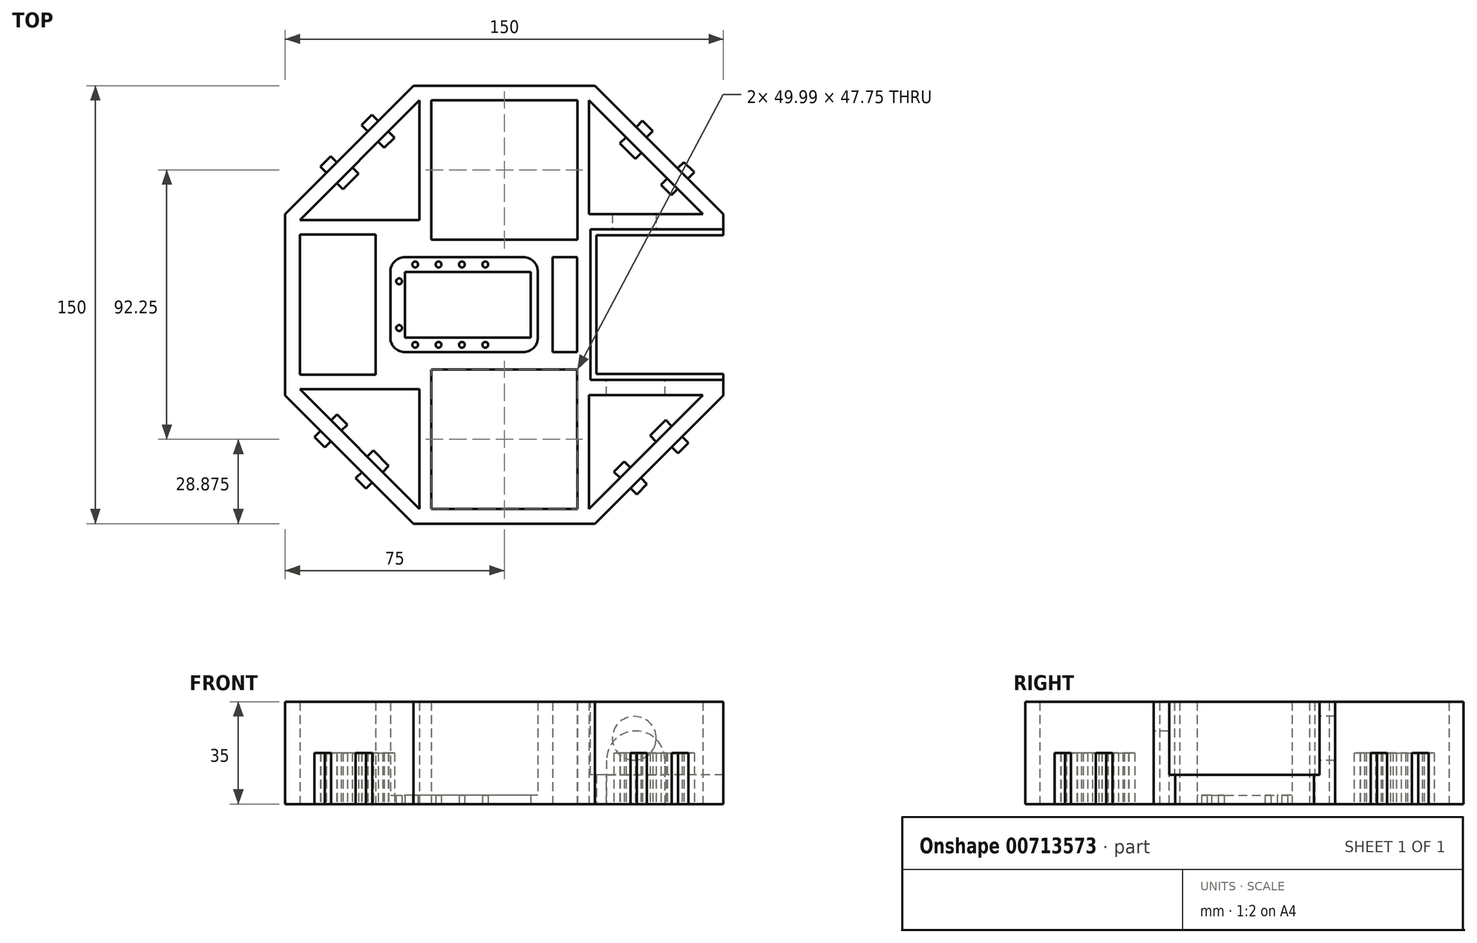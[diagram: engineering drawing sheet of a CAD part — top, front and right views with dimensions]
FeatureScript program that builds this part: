
annotation { "Feature Type Name" : "Feature", "Feature Type Description" : "" }
export const myFeature = defineFeature(function(context is Context, id is Id, definition is map)
    precondition{}
    {
        {
            var Q0;
            Q0=qCreatedBy(makeId("Top.planeOp"),FACE);
            var sketch = newSketch(context, id + "F0", { "sketchPlane" : qUnion([Q0])});
            skCircle(sketch, "E0.cCircle", {"center": v(0, 0) * mm, "radius": 75 * mm, "construction": true});
            skLineSegment(sketch, "E0.0", {"start": v(75, 31.07) * mm, "end": v(75, -31.07) * mm});
            skLineSegment(sketch, "E0.1", {"start": v(75, -31.07) * mm, "end": v(31.07, -75) * mm});
            skLineSegment(sketch, "E0.2", {"start": v(31.07, -75) * mm, "end": v(-31.07, -75) * mm});
            skLineSegment(sketch, "E0.3", {"start": v(-31.07, -75) * mm, "end": v(-75, -31.07) * mm});
            skLineSegment(sketch, "E0.4", {"start": v(-75, -31.07) * mm, "end": v(-75, 31.07) * mm});
            skLineSegment(sketch, "E0.5", {"start": v(-75, 31.07) * mm, "end": v(-31.07, 75) * mm});
            skLineSegment(sketch, "E0.6", {"start": v(-31.07, 75) * mm, "end": v(31.07, 75) * mm});
            skLineSegment(sketch, "E0.7", {"start": v(31.07, 75) * mm, "end": v(75, 31.07) * mm});
            skPoint(sketch, "E0.0.midPoint", {"position": v(75, 0) * mm});
            skLineSegment(sketch, "E1", {"start": v(0, 0) * mm, "end": v(11.5, 0) * mm, "construction": true});
            skLineSegment(sketch, "E2", {"start": v(11.5, 0) * mm, "end": v(11.5, -16.25) * mm});
            skLineSegment(sketch, "E3", {"start": v(11.5, 0) * mm, "end": v(11.5, 16.25) * mm});
            skLineSegment(sketch, "E4", {"start": v(11.5, 16.25) * mm, "end": v(-39, 16.25) * mm});
            skLineSegment(sketch, "E5", {"start": v(11.5, -16.25) * mm, "end": v(-39, -16.25) * mm});
            skLineSegment(sketch, "E6", {"start": v(-39, 16.25) * mm, "end": v(-39, -16.25) * mm});
            skSolve(sketch);
        }
        {
            var Q0;
            Q0=qSketchRegion(id+"F0",true);
            extrude(context, id + "F1", {"entities" : qUnion([Q0]), "depth" : 35 * mm});
        }
        {
            var Q0;
            Q0=makeQuery(id+"F1.opExtrude","CAP_FACE",FACE,{"disambiguationData":[OSD([sQuery(id+"F0.wireOp",EDGE,"E0.0"),sQuery(id+"F0.wireOp",EDGE,"E0.1"),sQuery(id+"F0.wireOp",EDGE,"E0.2"),sQuery(id+"F0.wireOp",EDGE,"E0.3"),sQuery(id+"F0.wireOp",EDGE,"E0.4"),sQuery(id+"F0.wireOp",EDGE,"E0.5"),sQuery(id+"F0.wireOp",EDGE,"E0.6"),sQuery(id+"F0.wireOp",EDGE,"E0.7"),sQuery(id+"F0.wireOp",EDGE,"E2"),sQuery(id+"F0.wireOp",EDGE,"E3"),sQuery(id+"F0.wireOp",EDGE,"E4"),sQuery(id+"F0.wireOp",EDGE,"E5"),sQuery(id+"F0.wireOp",EDGE,"E6")])],"isStart":true});
            var sketch = newSketch(context, id + "F2", { "sketchPlane" : qUnion([Q0])});
            skLineSegment(sketch, "E7.0", {"start": v(31.07, 75) * mm, "end": v(-31.07, 75) * mm});
            skLineSegment(sketch, "E7.1", {"start": v(-31.07, 75) * mm, "end": v(-75, 31.07) * mm});
            skLineSegment(sketch, "E7.2", {"start": v(-75, 31.07) * mm, "end": v(-75, -31.07) * mm});
            skLineSegment(sketch, "E7.3", {"start": v(-75, -31.07) * mm, "end": v(-31.07, -75) * mm});
            skLineSegment(sketch, "E7.4", {"start": v(-31.07, -75) * mm, "end": v(31.07, -75) * mm});
            skLineSegment(sketch, "E7.5", {"start": v(31.07, -75) * mm, "end": v(75, -31.07) * mm});
            skLineSegment(sketch, "E7.6", {"start": v(75, -31.07) * mm, "end": v(75, 31.07) * mm});
            skLineSegment(sketch, "E7.7", {"start": v(75, 31.07) * mm, "end": v(31.07, 75) * mm});
            skLineSegment(sketch, "E8.0", {"start": v(-29, 70) * mm, "end": v(-70, 29) * mm});
            skLineSegment(sketch, "E8.1", {"start": v(29, 70) * mm, "end": v(-29, 70) * mm, "construction": true});
            skLineSegment(sketch, "E8.2", {"start": v(-70, 29) * mm, "end": v(-70, -29) * mm, "construction": true});
            skLineSegment(sketch, "E8.3", {"start": v(70, 29) * mm, "end": v(68, 31) * mm, "construction": true});
            skLineSegment(sketch, "E8.4", {"start": v(-70, -29) * mm, "end": v(-29, -70) * mm});
            skLineSegment(sketch, "E8.5", {"start": v(-29, -70) * mm, "end": v(29, -70) * mm, "construction": true});
            skLineSegment(sketch, "E8.6", {"start": v(29, -70) * mm, "end": v(68, -31) * mm});
            skLineSegment(sketch, "E8.7", {"start": v(70, -29) * mm, "end": v(70, 29) * mm, "construction": true});
            skLineSegment(sketch, "E9.0", {"start": v(11.5, 16.25) * mm, "end": v(-39, 16.25) * mm, "construction": true});
            skLineSegment(sketch, "E9.1", {"start": v(-39, -16.25) * mm, "end": v(-39, 16.25) * mm, "construction": true});
            skLineSegment(sketch, "E9.2", {"start": v(11.5, -16.25) * mm, "end": v(-39, -16.25) * mm, "construction": true});
            skLineSegment(sketch, "E9.3", {"start": v(11.5, 16.25) * mm, "end": v(11.5, -16.25) * mm, "construction": true});
            skLineSegment(sketch, "E10", {"start": v(-70, 29) * mm, "end": v(-29, 29) * mm});
            skLineSegment(sketch, "E11", {"start": v(-29, 70) * mm, "end": v(-29, 29) * mm});
            skLineSegment(sketch, "E12", {"start": v(29, 70) * mm, "end": v(29, 31) * mm});
            skLineSegment(sketch, "E13", {"start": v(29, 29) * mm, "end": v(70, 29) * mm, "construction": true});
            skLineSegment(sketch, "E14", {"start": v(70, -29) * mm, "end": v(29, -29) * mm, "construction": true});
            skLineSegment(sketch, "E15", {"start": v(29, -29) * mm, "end": v(29, -31) * mm, "construction": true});
            skLineSegment(sketch, "E16", {"start": v(-29, -70) * mm, "end": v(-29, -29) * mm});
            skLineSegment(sketch, "E17", {"start": v(-29, -29) * mm, "end": v(-70, -29) * mm});
            skLineSegment(sketch, "E18", {"start": v(-25, 70) * mm, "end": v(25, 70) * mm});
            skLineSegment(sketch, "E19", {"start": v(0, 0) * mm, "end": v(27.89, 0) * mm, "construction": true});
            skPoint(sketch, "E19.endSnap0", {"position": v(11.5, 0) * mm});
            skLineSegment(sketch, "E20.MirrorCS", {"start": v(-25, -70) * mm, "end": v(25, -70) * mm});
            skLineSegment(sketch, "E21", {"start": v(-44, 24) * mm, "end": v(-44, -24) * mm});
            skLineSegment(sketch, "E22.0", {"start": v(68, -31) * mm, "end": v(29, -31) * mm});
            skLineSegment(sketch, "E23", {"start": v(29, -31) * mm, "end": v(29, -70) * mm});
            skLineSegment(sketch, "E24", {"start": v(68, -31) * mm, "end": v(70, -29) * mm, "construction": true});
            skLineSegment(sketch, "E25.0", {"start": v(29, 31) * mm, "end": v(68, 31) * mm});
            skLineSegment(sketch, "E26", {"start": v(29, 31) * mm, "end": v(29, 29) * mm, "construction": true});
            skLineSegment(sketch, "E27", {"start": v(68, 31) * mm, "end": v(29, 70) * mm});
            skLineSegment(sketch, "E28", {"start": v(-44, 24) * mm, "end": v(-70, 24) * mm});
            skLineSegment(sketch, "E29", {"start": v(-44, -24) * mm, "end": v(-70, -24) * mm});
            skLineSegment(sketch, "E30", {"start": v(-70, -24) * mm, "end": v(-70, 24) * mm});
            skLineSegment(sketch, "E31", {"start": v(-25, 22.25) * mm, "end": v(24.98, 22.25) * mm});
            skLineSegment(sketch, "E32", {"start": v(-25, -22.25) * mm, "end": v(25, -22.25) * mm});
            skLineSegment(sketch, "E33", {"start": v(-25, -22.25) * mm, "end": v(-25, -70) * mm});
            skLineSegment(sketch, "E34", {"start": v(25, -22.25) * mm, "end": v(25, -70) * mm});
            skLineSegment(sketch, "E35", {"start": v(24.98, 22.25) * mm, "end": v(25, 70) * mm});
            skLineSegment(sketch, "E36", {"start": v(-25, 22.25) * mm, "end": v(-25, 70) * mm});
            skLineSegment(sketch, "E37", {"start": v(16.5, 16.25) * mm, "end": v(16.5, -16.25) * mm});
            skLineSegment(sketch, "E38", {"start": v(16.5, 16.25) * mm, "end": v(24.98, 16.25) * mm});
            skLineSegment(sketch, "E39", {"start": v(24.98, 16.25) * mm, "end": v(24.98, -16.25) * mm});
            skLineSegment(sketch, "E40", {"start": v(24.98, -16.25) * mm, "end": v(16.5, -16.25) * mm});
            skSolve(sketch);
        }
        {
            var Q0;
            Q0=makeQuery(id+"F2.imprint","IMPRINT",FACE,{"disambiguationData":[TD([[makeQuery(id+"F2.imprint","IMPRINT",EDGE,{"derivedFrom":sQuery(id+"F2.wireOp",EDGE,"E8.0")}),1.0]])]});
            var Q1;
            Q1=makeQuery(id+"F2.imprint","IMPRINT",FACE,{"disambiguationData":[TD([[makeQuery(id+"F2.imprint","IMPRINT",EDGE,{"derivedFrom":sQuery(id+"F2.wireOp",EDGE,"E8.3")}),1.0]])]});
            var Q2;
            Q2=makeQuery(id+"F2.imprint","IMPRINT",FACE,{"disambiguationData":[TD([[makeQuery(id+"F2.imprint","IMPRINT",EDGE,{"derivedFrom":sQuery(id+"F2.wireOp",EDGE,"E8.4")}),1.0]])]});
            var Q3;
            Q3=makeQuery(id+"F2.imprint","IMPRINT",FACE,{"disambiguationData":[TD([[makeQuery(id+"F2.imprint","IMPRINT",EDGE,{"derivedFrom":sQuery(id+"F2.wireOp",EDGE,"8fvEKYef-Aid4-GxJZ-9eho-uKyJXPdf4iPF")}),1.0]])]});
            var Q4;
            Q4=makeQuery(id+"F2.imprint","IMPRINT",FACE,{"disambiguationData":[TD([[makeQuery(id+"F2.imprint","IMPRINT",EDGE,{"derivedFrom":sQuery(id+"F2.wireOp",EDGE,"9003354b-389c-4ee3-9b45-5ecd4443ff8f0.MirrorCS")}),-1.0]])]});
            var Q5;
            Q5=makeQuery(id+"F2.imprint","IMPRINT",FACE,{"disambiguationData":[TD([[makeQuery(id+"F2.imprint","IMPRINT",EDGE,{"derivedFrom":sQuery(id+"F2.wireOp",EDGE,"X22rCwxT-IPlS-Nedg-AixG-TADrHZbppUWM")}),-1.0]])]});
            var Q6;
            Q6=makeQuery(id+"F2.imprint","IMPRINT",FACE,{"disambiguationData":[TD([[makeQuery(id+"F2.imprint","IMPRINT",EDGE,{"derivedFrom":sQuery(id+"F2.wireOp",EDGE,"E12")}),1.0]])]});
            var Q7;
            Q7=makeQuery(id+"F2.imprint","IMPRINT",FACE,{"disambiguationData":[TD([[makeQuery(id+"F2.imprint","IMPRINT",EDGE,{"derivedFrom":sQuery(id+"F2.wireOp",EDGE,"E8.6")}),1.0]])]});
            var Q8;
            Q8=makeQuery(id+"F2.imprint","IMPRINT",FACE,{"disambiguationData":[TD([[makeQuery(id+"F2.imprint","IMPRINT",EDGE,{"derivedFrom":sQuery(id+"F2.wireOp",EDGE,"E21")}),-1.0]])]});
            var Q9;
            Q9=makeQuery(id+"F2.imprint","IMPRINT",FACE,{"disambiguationData":[TD([[makeQuery(id+"F2.imprint","IMPRINT",EDGE,{"derivedFrom":sQuery(id+"F2.wireOp",EDGE,"E18")}),-1.0]])]});
            var Q10;
            Q10=makeQuery(id+"F2.imprint","IMPRINT",FACE,{"disambiguationData":[TD([[makeQuery(id+"F2.imprint","IMPRINT",EDGE,{"derivedFrom":sQuery(id+"F2.wireOp",EDGE,"E20.MirrorCS")}),1.0]])]});
            var Q11;
            Q11=makeQuery(id+"F2.imprint","IMPRINT",FACE,{"disambiguationData":[TD([[makeQuery(id+"F2.imprint","IMPRINT",EDGE,{"derivedFrom":sQuery(id+"F2.wireOp",EDGE,"E37")}),1.0]])]});
            extrude(context, id + "F3", {"entities" : qUnion([Q0, Q1, Q2, Q3, Q4, Q5, Q6, Q7, Q8, Q9, Q10, Q11]), "operationType" : NewBodyOperationType.REMOVE, "oppositeDirection" : true, "depth" : 36.9 * mm});
        }
        {
            var Q0;
            Q0=makeQuery(id+"F1.opExtrude","CAP_FACE",FACE,{"disambiguationData":[OSD([sQuery(id+"F0.wireOp",EDGE,"E0.0"),sQuery(id+"F0.wireOp",EDGE,"E0.1"),sQuery(id+"F0.wireOp",EDGE,"E0.2"),sQuery(id+"F0.wireOp",EDGE,"E0.3"),sQuery(id+"F0.wireOp",EDGE,"E0.4"),sQuery(id+"F0.wireOp",EDGE,"E0.5"),sQuery(id+"F0.wireOp",EDGE,"E0.6"),sQuery(id+"F0.wireOp",EDGE,"E0.7"),sQuery(id+"F0.wireOp",EDGE,"E2"),sQuery(id+"F0.wireOp",EDGE,"E3"),sQuery(id+"F0.wireOp",EDGE,"E4"),sQuery(id+"F0.wireOp",EDGE,"E5"),sQuery(id+"F0.wireOp",EDGE,"E6")])],"isStart":true});
            var sketch = newSketch(context, id + "F4", { "sketchPlane" : qUnion([Q0])});
            skLineSegment(sketch, "E41.0", {"start": v(-39, -16.25) * mm, "end": v(-39, 16.25) * mm});
            skLineSegment(sketch, "E41.1", {"start": v(11.5, 16.25) * mm, "end": v(-39, 16.25) * mm});
            skLineSegment(sketch, "E41.2", {"start": v(11.5, -16.25) * mm, "end": v(-39, -16.25) * mm});
            skLineSegment(sketch, "E41.3", {"start": v(11.5, 16.25) * mm, "end": v(11.5, -16.25) * mm});
            skLineSegment(sketch, "E42.0", {"start": v(9, -11.25) * mm, "end": v(-34, -11.25) * mm});
            skLineSegment(sketch, "E42.1", {"start": v(-34, -11.25) * mm, "end": v(-34, 11.25) * mm});
            skLineSegment(sketch, "E42.2", {"start": v(9, 11.25) * mm, "end": v(-34, 11.25) * mm});
            skLineSegment(sketch, "E43", {"start": v(-39, 13.75) * mm, "end": v(-30.5, 13.75) * mm, "construction": true});
            skLineSegment(sketch, "E44", {"start": v(-30.5, 13.75) * mm, "end": v(-22.5, 13.75) * mm, "construction": true});
            skLineSegment(sketch, "E45", {"start": v(-22.5, 13.75) * mm, "end": v(-14.5, 13.75) * mm, "construction": true});
            skLineSegment(sketch, "E46", {"start": v(-14.5, 13.75) * mm, "end": v(-6.5, 13.75) * mm, "construction": true});
            skCircle(sketch, "E47", {"center": v(-30.5, 13.75) * mm, "radius": 1 * mm});
            skCircle(sketch, "E48", {"center": v(-22.5, 13.75) * mm, "radius": 1 * mm});
            skCircle(sketch, "E49", {"center": v(-14.5, 13.75) * mm, "radius": 1 * mm});
            skCircle(sketch, "E50", {"center": v(-6.5, 13.75) * mm, "radius": 1 * mm});
            skLineSegment(sketch, "E51", {"start": v(-39, 0) * mm, "end": v(-36, 0) * mm, "construction": true});
            skPoint(sketch, "E51.endSnap0", {"position": v(-39, 0) * mm});
            skLineSegment(sketch, "E52", {"start": v(-36, 0) * mm, "end": v(-36, 8) * mm, "construction": true});
            skLineSegment(sketch, "E53", {"start": v(-36, 0) * mm, "end": v(-36, -8) * mm, "construction": true});
            skLineSegment(sketch, "E54.MirrorCS", {"start": v(-39, -13.75) * mm, "end": v(-30.5, -13.75) * mm, "construction": true});
            skLineSegment(sketch, "E55.MirrorCS", {"start": v(-14.5, -13.75) * mm, "end": v(-6.5, -13.75) * mm, "construction": true});
            skCircle(sketch, "E56.MirrorC", {"center": v(-22.5, -13.75) * mm, "radius": 1 * mm});
            skCircle(sketch, "E57.MirrorC", {"center": v(-6.5, -13.75) * mm, "radius": 1 * mm});
            skCircle(sketch, "E58.MirrorC", {"center": v(-30.5, -13.75) * mm, "radius": 1 * mm});
            skLineSegment(sketch, "E59.MirrorCS", {"start": v(-30.5, -13.75) * mm, "end": v(-22.5, -13.75) * mm, "construction": true});
            skLineSegment(sketch, "E60.MirrorCS", {"start": v(-22.5, -13.75) * mm, "end": v(-14.5, -13.75) * mm, "construction": true});
            skCircle(sketch, "E61.MirrorC", {"center": v(-14.5, -13.75) * mm, "radius": 1 * mm});
            skCircle(sketch, "E62", {"center": v(-36, 8) * mm, "radius": 1 * mm});
            skCircle(sketch, "E63", {"center": v(-36, -8) * mm, "radius": 1 * mm});
            skLineSegment(sketch, "E64.0", {"start": v(9, 11.25) * mm, "end": v(9, -11.25) * mm});
            skSolve(sketch);
        }
        {
            var Q0;
            Q0=makeQuery(id+"F4.imprint","IMPRINT",FACE,{"disambiguationData":[TD([[makeQuery(id+"F4.imprint","IMPRINT",EDGE,{"derivedFrom":sQuery(id+"F4.wireOp",EDGE,"E41.0")}),-1.0]])]});
            extrude(context, id + "F5", {"entities" : qUnion([Q0]), "operationType" : NewBodyOperationType.ADD, "oppositeDirection" : true, "depth" : 3 * mm});
        }
        {
            var Q0;
            Q0=makeQuery(id+"F1.opExtrude","SWEPT_EDGE",EDGE,{"disambiguationData":[OSD([sQuery(id+"F0.wireOp",EDGE,"E5"),sQuery(id+"F0.wireOp",EDGE,"E6")])]});
            var Q1;
            Q1=makeQuery(id+"F1.opExtrude","SWEPT_EDGE",EDGE,{"disambiguationData":[OSD([sQuery(id+"F0.wireOp",EDGE,"E4"),sQuery(id+"F0.wireOp",EDGE,"E6")])]});
            var Q2;
            Q2=makeQuery(id+"F1.opExtrude","SWEPT_EDGE",EDGE,{"disambiguationData":[OSD([sQuery(id+"F0.wireOp",EDGE,"E3"),sQuery(id+"F0.wireOp",EDGE,"E4")])]});
            var Q3;
            Q3=makeQuery(id+"F1.opExtrude","SWEPT_EDGE",EDGE,{"disambiguationData":[OSD([sQuery(id+"F0.wireOp",EDGE,"E2"),sQuery(id+"F0.wireOp",EDGE,"E5")])]});
            fillet(context, id + "F6", {"entities" : qUnion([Q0, Q1, Q2, Q3]), "radius" : 5 * mm, "tangentPropagation" : true, "allowEdgeOverflow" : false});
        }
        {
            var Q0;
            Q0=makeQuery(id+"F1.opExtrude","CAP_FACE",FACE,{"disambiguationData":[OSD([sQuery(id+"F0.wireOp",EDGE,"E0.0"),sQuery(id+"F0.wireOp",EDGE,"E0.1"),sQuery(id+"F0.wireOp",EDGE,"E0.2"),sQuery(id+"F0.wireOp",EDGE,"E0.3"),sQuery(id+"F0.wireOp",EDGE,"E0.4"),sQuery(id+"F0.wireOp",EDGE,"E0.5"),sQuery(id+"F0.wireOp",EDGE,"E0.6"),sQuery(id+"F0.wireOp",EDGE,"E0.7"),sQuery(id+"F0.wireOp",EDGE,"E2"),sQuery(id+"F0.wireOp",EDGE,"E3"),sQuery(id+"F0.wireOp",EDGE,"E4"),sQuery(id+"F0.wireOp",EDGE,"E5"),sQuery(id+"F0.wireOp",EDGE,"E6")])],"isStart":false});
            var sketch = newSketch(context, id + "F7", { "sketchPlane" : qUnion([Q0])});
            skLineSegment(sketch, "E65.bottom", {"start": v(75, -25.75) * mm, "end": v(29.5, -25.75) * mm});
            skLineSegment(sketch, "E65.top", {"start": v(75, 25.75) * mm, "end": v(29.5, 25.75) * mm});
            skLineSegment(sketch, "E65.right", {"start": v(29.5, -25.75) * mm, "end": v(29.5, 25.75) * mm});
            skPoint(sketch, "E65.middle", {"position": v(52.25, 0) * mm});
            skPoint(sketch, "E66", {"position": v(75, 0) * mm});
            skLineSegment(sketch, "E67", {"start": v(75, 0) * mm, "end": v(52.25, 0) * mm, "construction": true});
            skSolve(sketch);
        }
        {
            var Q0;
            {var subQ0=sQuery(id+"F7.wireOp",EDGE,"E65.bottom");Q0=makeQuery(id+"F7.imprint","IMPRINT",FACE,{"disambiguationData":[TD([[makeQuery(id+"F7.imprint","IMPRINT",EDGE,{"derivedFrom":subQ0}),-1.0]])]});}
            extrude(context, id + "F8", {"entities" : qUnion([Q0]), "operationType" : NewBodyOperationType.REMOVE, "oppositeDirection" : true, "depth" : 30 * mm});
        }
        {
            var Q0;
            Q0=makeQuery(id+"F8.boolean.opBoolean","COPY",FACE,{"derivedFrom":makeQuery(id+"F8.opExtrude","CAP_FACE",FACE,{"disambiguationData":[OSD([sQuery(id+"F0.wireOp",EDGE,"E0.0"),sQuery(id+"F7.wireOp",EDGE,"E65.bottom"),sQuery(id+"F7.wireOp",EDGE,"E65.top"),sQuery(id+"F7.wireOp",EDGE,"E65.right")])],"isStart":false})});
            var sketch = newSketch(context, id + "F9", { "sketchPlane" : qUnion([Q0])});
            skLineSegment(sketch, "E68.0", {"start": v(75, 25.75) * mm, "end": v(29.5, 25.75) * mm});
            skLineSegment(sketch, "E68.1", {"start": v(29.5, -25.75) * mm, "end": v(29.5, 25.75) * mm});
            skLineSegment(sketch, "E68.2", {"start": v(75, -25.75) * mm, "end": v(29.5, -25.75) * mm});
            skLineSegment(sketch, "E69.0", {"start": v(75, -23.75) * mm, "end": v(31.5, -23.75) * mm});
            skLineSegment(sketch, "E69.1", {"start": v(31.5, -23.75) * mm, "end": v(31.5, 23.75) * mm});
            skLineSegment(sketch, "E69.2", {"start": v(75, 23.75) * mm, "end": v(31.5, 23.75) * mm});
            skLineSegment(sketch, "E70", {"start": v(75, 23.75) * mm, "end": v(75, 25.75) * mm});
            skLineSegment(sketch, "E71", {"start": v(75, -23.75) * mm, "end": v(75, -25.75) * mm});
            skSolve(sketch);
        }
        {
            var Q0;
            Q0=makeQuery(id+"F9.imprint","IMPRINT",FACE,{"disambiguationData":[TD([[makeQuery(id+"F9.imprint","IMPRINT",EDGE,{"derivedFrom":sQuery(id+"F9.wireOp",EDGE,"E68.0")}),1.0]])]});
            extrude(context, id + "F10", {"entities" : qUnion([Q0]), "operationType" : NewBodyOperationType.ADD, "depth" : 5 * mm});
        }
        {
            var Q0;
            Q0=makeQuery(id+"F8.boolean.opBoolean","COPY",FACE,{"derivedFrom":makeQuery(id+"F8.opExtrude","SWEPT_FACE",FACE,{"disambiguationData":[OSD([sQuery(id+"F7.wireOp",EDGE,"E65.bottom")])]})});
            var sketch = newSketch(context, id + "F11", { "sketchPlane" : qUnion([Q0])});
            skLineSegment(sketch, "E72.0", {"start": v(-68, 35) * mm, "end": v(-68, 0) * mm, "construction": true});
            skLineSegment(sketch, "E73", {"start": v(-55, 10) * mm, "end": v(-55, 25) * mm});
            skLineSegment(sketch, "E74", {"start": v(-55, 25) * mm, "end": v(-35, 25) * mm});
            skLineSegment(sketch, "E75", {"start": v(-35, 25) * mm, "end": v(-35, 10) * mm});
            skLineSegment(sketch, "E76", {"start": v(-35, 10) * mm, "end": v(-55, 10) * mm});
            skSolve(sketch);
        }
        {
            var Q0;
            Q0=makeQuery(id+"F11.imprint","IMPRINT",FACE,{"disambiguationData":[TD([[makeQuery(id+"F11.imprint","IMPRINT",EDGE,{"derivedFrom":sQuery(id+"F11.wireOp",EDGE,"E73")}),-1.0]])]});
            extrude(context, id + "F12", {"entities" : qUnion([Q0]), "operationType" : NewBodyOperationType.REMOVE, "oppositeDirection" : true, "depth" : 11.4 * mm});
        }
        {
            var Q0;
            Q0=makeQuery(id+"F12.boolean.opBoolean","COPY",EDGE,{"derivedFrom":makeQuery(id+"F12.opExtrude","SWEPT_EDGE",EDGE,{"disambiguationData":[OSD([sQuery(id+"F11.wireOp",EDGE,"E73"),sQuery(id+"F11.wireOp",EDGE,"E74")])]})});
            var Q1;
            Q1=makeQuery(id+"F12.boolean.opBoolean","COPY",EDGE,{"derivedFrom":makeQuery(id+"F12.opExtrude","SWEPT_EDGE",EDGE,{"disambiguationData":[OSD([sQuery(id+"F11.wireOp",EDGE,"E74"),sQuery(id+"F11.wireOp",EDGE,"E75")])]})});
            fillet(context, id + "F13", {"entities" : qUnion([Q0, Q1]), "radius" : 10 * mm, "tangentPropagation" : true, "allowEdgeOverflow" : false});
        }
        {
            var Q0;
            Q0=makeQuery(id+"F12.boolean.opBoolean","MERGE",FACE,{"derivedFrom":[makeQuery(id+"F10.opExtrude","CAP_FACE",FACE,{"disambiguationData":[OSD([sQuery(id+"F9.wireOp",EDGE,"E68.0"),sQuery(id+"F9.wireOp",EDGE,"E68.1"),sQuery(id+"F9.wireOp",EDGE,"E68.2"),sQuery(id+"F9.wireOp",EDGE,"E69.0"),sQuery(id+"F9.wireOp",EDGE,"E69.1"),sQuery(id+"F9.wireOp",EDGE,"E69.2"),sQuery(id+"F9.wireOp",EDGE,"E70"),sQuery(id+"F9.wireOp",EDGE,"E71")])],"isStart":false}),makeQuery(id+"F12.opExtrude","SWEPT_FACE",FACE,{"disambiguationData":[OSD([sQuery(id+"F11.wireOp",EDGE,"E76")])]})]});
            var sketch = newSketch(context, id + "F14", { "sketchPlane" : qUnion([Q0])});
            skLineSegment(sketch, "E77", {"start": v(35, -31) * mm, "end": v(35, -25.75) * mm});
            skLineSegment(sketch, "E78", {"start": v(35, -25.75) * mm, "end": v(55, -25.75) * mm});
            skLineSegment(sketch, "E79", {"start": v(55, -25.75) * mm, "end": v(55, -31) * mm});
            skLineSegment(sketch, "E80", {"start": v(55, -31) * mm, "end": v(35, -31) * mm});
            skSolve(sketch);
        }
        {
            var Q0;
            Q0=makeQuery(id+"F14.imprint","IMPRINT",FACE,{"disambiguationData":[TD([[makeQuery(id+"F14.imprint","IMPRINT",EDGE,{"derivedFrom":sQuery(id+"F14.wireOp",EDGE,"E77")}),-1.0]])]});
            extrude(context, id + "F15", {"entities" : qUnion([Q0]), "operationType" : NewBodyOperationType.REMOVE, "oppositeDirection" : true, "depth" : 25 * mm});
        }
        {
            var Q0;
            Q0=makeQuery(id+"F8.boolean.opBoolean","COPY",FACE,{"derivedFrom":makeQuery(id+"F8.opExtrude","SWEPT_FACE",FACE,{"disambiguationData":[OSD([sQuery(id+"F7.wireOp",EDGE,"E65.top")])]})});
            var sketch = newSketch(context, id + "F16", { "sketchPlane" : qUnion([Q0])});
            skLineSegment(sketch, "E81", {"start": v(29.5, 22.5) * mm, "end": v(44.5, 22.5) * mm, "construction": true});
            skCircle(sketch, "E82", {"center": v(44.5, 22.5) * mm, "radius": 7.5 * mm});
            skSolve(sketch);
        }
        {
            var Q0;
            Q0=makeQuery(id+"F16.imprint","IMPRINT",FACE,{"disambiguationData":[TD([[makeQuery(id+"F16.imprint","IMPRINT",EDGE,{"derivedFrom":sQuery(id+"F16.wireOp",EDGE,"E82")}),1.0]])]});
            extrude(context, id + "F17", {"entities" : qUnion([Q0]), "operationType" : NewBodyOperationType.REMOVE, "oppositeDirection" : true, "depth" : 7.7 * mm});
        }
        {
            var Q0;
            Q0=makeQuery(id+"F8.boolean.opBoolean","COPY",FACE,{"derivedFrom":makeQuery(id+"F8.opExtrude","CAP_FACE",FACE,{"disambiguationData":[OSD([sQuery(id+"F0.wireOp",EDGE,"E0.0"),sQuery(id+"F7.wireOp",EDGE,"E65.bottom"),sQuery(id+"F7.wireOp",EDGE,"E65.top"),sQuery(id+"F7.wireOp",EDGE,"E65.right")])],"isStart":false})});
            extrude(context, id + "F18", {"entities" : qUnion([Q0]), "operationType" : NewBodyOperationType.REMOVE, "oppositeDirection" : true, "depth" : 25 * mm});
        }
        {
            var Q0;
            Q0=qCreatedBy(makeId("Top.planeOp"),FACE);
            var sketch = newSketch(context, id + "F19", { "sketchPlane" : qUnion([Q0])});
            skPoint(sketch, "E83.0", {"position": v(48.5, -50.5) * mm});
            skLineSegment(sketch, "E84.0", {"start": v(68, -31) * mm, "end": v(29, -70) * mm, "construction": true});
            skLineSegment(sketch, "E85", {"start": v(43.2, -55.8) * mm, "end": v(41.07, -53.68) * mm});
            skLineSegment(sketch, "E86", {"start": v(52.03, -46.96) * mm, "end": v(49.91, -44.84) * mm});
            skLineSegment(sketch, "E87", {"start": v(41.07, -53.68) * mm, "end": v(37.54, -57.21) * mm});
            skLineSegment(sketch, "E88", {"start": v(37.54, -57.21) * mm, "end": v(39.66, -59.34) * mm});
            skLineSegment(sketch, "E89", {"start": v(49.91, -44.84) * mm, "end": v(55.21, -39.54) * mm});
            skLineSegment(sketch, "E90", {"start": v(55.21, -39.54) * mm, "end": v(57.34, -41.66) * mm});
            skLineSegment(sketch, "E91", {"start": v(48.5, -50.5) * mm, "end": v(52.03, -54.03) * mm, "construction": true});
            skLineSegment(sketch, "E92.0", {"start": v(75, -31.07) * mm, "end": v(31.07, -75) * mm, "construction": true});
            skLineSegment(sketch, "E93", {"start": v(43.2, -55.8) * mm, "end": v(39.66, -59.34) * mm});
            skLineSegment(sketch, "E94", {"start": v(52.03, -46.96) * mm, "end": v(57.34, -41.66) * mm});
            skLineSegment(sketch, "E95", {"start": v(46.73, -59.34) * mm, "end": v(48.85, -61.46) * mm});
            skLineSegment(sketch, "E96", {"start": v(48.85, -61.46) * mm, "end": v(45.32, -65) * mm});
            skLineSegment(sketch, "E97", {"start": v(45.32, -65) * mm, "end": v(43.2, -62.87) * mm});
            skLineSegment(sketch, "E98", {"start": v(43.2, -62.87) * mm, "end": v(46.73, -59.34) * mm});
            skLineSegment(sketch, "E99", {"start": v(57.34, -48.73) * mm, "end": v(59.46, -50.85) * mm});
            skLineSegment(sketch, "E100", {"start": v(59.46, -50.85) * mm, "end": v(63, -47.32) * mm});
            skLineSegment(sketch, "E101", {"start": v(63, -47.32) * mm, "end": v(60.87, -45.2) * mm});
            skLineSegment(sketch, "E102", {"start": v(60.87, -45.2) * mm, "end": v(57.34, -48.73) * mm});
            skLineSegment(sketch, "E103.1.0", {"start": v(50.85, 59.46) * mm, "end": v(47.32, 63) * mm});
            skLineSegment(sketch, "E103.1.1", {"start": v(48.73, 57.34) * mm, "end": v(50.85, 59.46) * mm});
            skLineSegment(sketch, "E103.1.2", {"start": v(45.2, 60.87) * mm, "end": v(48.73, 57.34) * mm});
            skLineSegment(sketch, "E103.1.3", {"start": v(47.32, 63) * mm, "end": v(45.2, 60.87) * mm});
            skLineSegment(sketch, "E103.1.4", {"start": v(62.87, 43.2) * mm, "end": v(59.34, 46.73) * mm});
            skLineSegment(sketch, "E103.1.5", {"start": v(59.34, 46.73) * mm, "end": v(61.46, 48.85) * mm});
            skLineSegment(sketch, "E103.1.6", {"start": v(61.46, 48.85) * mm, "end": v(65, 45.32) * mm});
            skLineSegment(sketch, "E103.1.7", {"start": v(65, 45.32) * mm, "end": v(62.87, 43.2) * mm});
            skLineSegment(sketch, "E103.1.8", {"start": v(55.8, 43.2) * mm, "end": v(53.68, 41.07) * mm});
            skLineSegment(sketch, "E103.1.9", {"start": v(53.68, 41.07) * mm, "end": v(57.21, 37.54) * mm});
            skLineSegment(sketch, "E103.1.10", {"start": v(57.21, 37.54) * mm, "end": v(59.34, 39.66) * mm});
            skLineSegment(sketch, "E103.1.11", {"start": v(55.8, 43.2) * mm, "end": v(59.34, 39.66) * mm});
            skLineSegment(sketch, "E103.1.12", {"start": v(46.96, 52.03) * mm, "end": v(44.84, 49.91) * mm});
            skLineSegment(sketch, "E103.1.13", {"start": v(44.84, 49.91) * mm, "end": v(39.54, 55.21) * mm});
            skLineSegment(sketch, "E103.1.14", {"start": v(46.96, 52.03) * mm, "end": v(41.66, 57.34) * mm});
            skLineSegment(sketch, "E103.1.15", {"start": v(39.54, 55.21) * mm, "end": v(41.66, 57.34) * mm});
            skLineSegment(sketch, "E103.2.0", {"start": v(-59.46, 50.85) * mm, "end": v(-63, 47.32) * mm});
            skLineSegment(sketch, "E103.2.1", {"start": v(-57.34, 48.73) * mm, "end": v(-59.46, 50.85) * mm});
            skLineSegment(sketch, "E103.2.2", {"start": v(-60.87, 45.2) * mm, "end": v(-57.34, 48.73) * mm});
            skLineSegment(sketch, "E103.2.3", {"start": v(-63, 47.32) * mm, "end": v(-60.87, 45.2) * mm});
            skLineSegment(sketch, "E103.2.4", {"start": v(-43.2, 62.87) * mm, "end": v(-46.73, 59.34) * mm});
            skLineSegment(sketch, "E103.2.5", {"start": v(-46.73, 59.34) * mm, "end": v(-48.85, 61.46) * mm});
            skLineSegment(sketch, "E103.2.6", {"start": v(-48.85, 61.46) * mm, "end": v(-45.32, 65) * mm});
            skLineSegment(sketch, "E103.2.7", {"start": v(-45.32, 65) * mm, "end": v(-43.2, 62.87) * mm});
            skLineSegment(sketch, "E103.2.8", {"start": v(-43.2, 55.8) * mm, "end": v(-41.07, 53.68) * mm});
            skLineSegment(sketch, "E103.2.9", {"start": v(-41.07, 53.68) * mm, "end": v(-37.54, 57.21) * mm});
            skLineSegment(sketch, "E103.2.10", {"start": v(-37.54, 57.21) * mm, "end": v(-39.66, 59.34) * mm});
            skLineSegment(sketch, "E103.2.11", {"start": v(-43.2, 55.8) * mm, "end": v(-39.66, 59.34) * mm});
            skLineSegment(sketch, "E103.2.12", {"start": v(-52.03, 46.96) * mm, "end": v(-49.91, 44.84) * mm});
            skLineSegment(sketch, "E103.2.13", {"start": v(-49.91, 44.84) * mm, "end": v(-55.21, 39.54) * mm});
            skLineSegment(sketch, "E103.2.14", {"start": v(-52.03, 46.96) * mm, "end": v(-57.34, 41.66) * mm});
            skLineSegment(sketch, "E103.2.15", {"start": v(-55.21, 39.54) * mm, "end": v(-57.34, 41.66) * mm});
            skLineSegment(sketch, "E103.3.0", {"start": v(-50.85, -59.46) * mm, "end": v(-47.32, -63) * mm});
            skLineSegment(sketch, "E103.3.1", {"start": v(-48.73, -57.34) * mm, "end": v(-50.85, -59.46) * mm});
            skLineSegment(sketch, "E103.3.2", {"start": v(-45.2, -60.87) * mm, "end": v(-48.73, -57.34) * mm});
            skLineSegment(sketch, "E103.3.3", {"start": v(-47.32, -63) * mm, "end": v(-45.2, -60.87) * mm});
            skLineSegment(sketch, "E103.3.4", {"start": v(-62.87, -43.2) * mm, "end": v(-59.34, -46.73) * mm});
            skLineSegment(sketch, "E103.3.5", {"start": v(-59.34, -46.73) * mm, "end": v(-61.46, -48.85) * mm});
            skLineSegment(sketch, "E103.3.6", {"start": v(-61.46, -48.85) * mm, "end": v(-65, -45.32) * mm});
            skLineSegment(sketch, "E103.3.7", {"start": v(-65, -45.32) * mm, "end": v(-62.87, -43.2) * mm});
            skLineSegment(sketch, "E103.3.8", {"start": v(-55.8, -43.2) * mm, "end": v(-53.68, -41.07) * mm});
            skLineSegment(sketch, "E103.3.9", {"start": v(-53.68, -41.07) * mm, "end": v(-57.21, -37.54) * mm});
            skLineSegment(sketch, "E103.3.10", {"start": v(-57.21, -37.54) * mm, "end": v(-59.34, -39.66) * mm});
            skLineSegment(sketch, "E103.3.11", {"start": v(-55.8, -43.2) * mm, "end": v(-59.34, -39.66) * mm});
            skLineSegment(sketch, "E103.3.12", {"start": v(-46.96, -52.03) * mm, "end": v(-44.84, -49.91) * mm});
            skLineSegment(sketch, "E103.3.13", {"start": v(-44.84, -49.91) * mm, "end": v(-39.54, -55.21) * mm});
            skLineSegment(sketch, "E103.3.14", {"start": v(-46.96, -52.03) * mm, "end": v(-41.66, -57.34) * mm});
            skLineSegment(sketch, "E103.3.15", {"start": v(-39.54, -55.21) * mm, "end": v(-41.66, -57.34) * mm});
            skPoint(sketch, "E103.center", {"position": v(0, 0) * mm});
            skSolve(sketch);
        }
        {
            var Q0;
            Q0=qSketchRegion(id+"F19",true);
            extrude(context, id + "F20", {"entities" : qUnion([Q0]), "operationType" : NewBodyOperationType.ADD, "depth" : 17.5 * mm, "offsetDistance" : 25 * mm});
        }
    });
